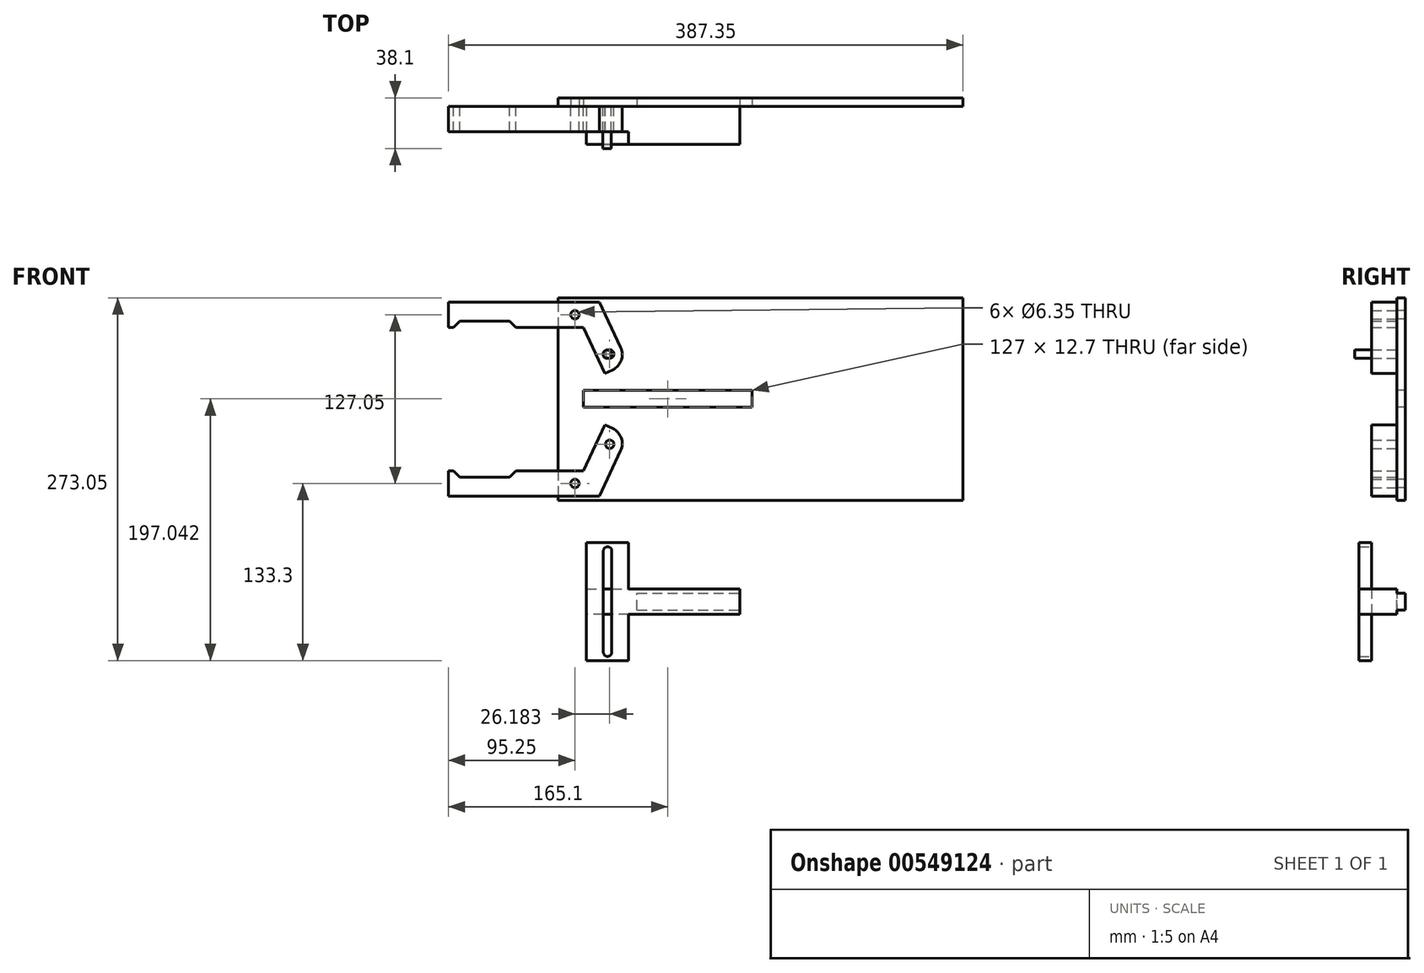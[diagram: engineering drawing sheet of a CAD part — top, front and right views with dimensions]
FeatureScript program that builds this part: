
annotation { "Feature Type Name" : "Feature", "Feature Type Description" : "" }
export const myFeature = defineFeature(function(context is Context, id is Id, definition is map)
    precondition{}
    {
        {
            var Q0;
            Q0=qCreatedBy(makeId("Front.planeOp"),FACE);
            var sketch = newSketch(context, id + "F0", { "sketchPlane" : qUnion([Q0])});
            skLineSegment(sketch, "E0.bottom", {"start": v(-95.25, 9.53) * mm, "end": v(18.49, 9.53) * mm});
            skLineSegment(sketch, "E0.top", {"start": v(-95.25, -9.52) * mm, "end": v(-91.44, -9.52) * mm});
            skLineSegment(sketch, "E0.left", {"start": v(-95.25, 9.53) * mm, "end": v(-95.25, -9.52) * mm});
            skLineSegment(sketch, "E1", {"start": v(6.35, -9.52) * mm, "end": v(22.5, -44.18) * mm});
            skLineSegment(sketch, "E2", {"start": v(22.5, -44.18) * mm, "end": v(39.77, -36.13) * mm});
            skLineSegment(sketch, "E3", {"start": v(18.49, 9.53) * mm, "end": v(39.77, -36.13) * mm});
            skCircle(sketch, "E4", {"center": v(0, 0) * mm, "radius": 3.18 * mm});
            skLineSegment(sketch, "E5", {"start": v(31.14, -40.15) * mm, "end": v(7.98, 9.53) * mm, "construction": true});
            skCircle(sketch, "E6", {"center": v(26.18, -29.52) * mm, "radius": 3.18 * mm});
            skLineSegment(sketch, "E7", {"start": v(-91.44, -9.53) * mm, "end": v(-86.6, -4.68) * mm});
            skLineSegment(sketch, "E8", {"start": v(-86.6, -4.68) * mm, "end": v(-49.3, -4.68) * mm});
            skLineSegment(sketch, "E9", {"start": v(-49.3, -4.68) * mm, "end": v(-44.45, -9.52) * mm});
            skLineSegment(sketch, "E10", {"start": v(-44.45, -9.52) * mm, "end": v(-44.45, -9.52) * mm});
            skLineSegment(sketch, "E11", {"start": v(-44.45, -9.52) * mm, "end": v(6.35, -9.52) * mm});
            skSolve(sketch);
        }
        {
            var Q0;
            Q0 = qSketchRegion(id + "F0", true);
            extrude(context, id + "F1", {"entities" : qUnion([Q0]), "depth" : 19.05 * mm, "offsetDistance" : 25.4 * mm});
        }
        {
            var Q0;
            Q0=qCreatedBy(makeId("Front.planeOp"),FACE);
            var sketch = newSketch(context, id + "F2", { "sketchPlane" : qUnion([Q0])});
            skLineSegment(sketch, "E12", {"start": v(0, 0) * mm, "end": v(0, -127) * mm, "construction": true});
            skLineSegment(sketch, "E13", {"start": v(0, -63.5) * mm, "end": v(127, -63.5) * mm, "construction": true});
            skSolve(sketch);
        }
        {
            var Q0;
            Q0=qCreatedBy(makeId("Top.planeOp"),FACE);
            cPlane(context, id + "F3", {"entities" : qUnion([Q0]), "cplaneType" : CPlaneType.OFFSET, "offset" : 63.5 * mm, "oppositeDirection" : true, "width" : 152.4 * mm, "height" : 152.4 * mm});
        }
        {
            var Q0;
            Q0=makeQuery(id+"F1.opExtrude","SWEPT_BODY",BODY,{"disambiguationData":[OSD([sQuery(id+"F0.wireOp",EDGE,"E0.bottom"),sQuery(id+"F0.wireOp",EDGE,"E0.top"),sQuery(id+"F0.wireOp",EDGE,"E0.left"),sQuery(id+"F0.wireOp",EDGE,"E1"),sQuery(id+"F0.wireOp",EDGE,"E2"),sQuery(id+"F0.wireOp",EDGE,"E3"),sQuery(id+"F0.wireOp",EDGE,"E4"),sQuery(id+"F0.wireOp",EDGE,"E6"),sQuery(id+"F0.wireOp",EDGE,"E7"),sQuery(id+"F0.wireOp",EDGE,"E8"),sQuery(id+"F0.wireOp",EDGE,"E9"),sQuery(id+"F0.wireOp",EDGE,"E11")])]});
            var Q1;
            Q1=qCreatedBy(id+"F3.planeOp",FACE);
            mirror(context, id + "F4", {"entities" : qUnion([Q0]), "mirrorPlane" : qUnion([Q1])});
        }
        {
            var Q0;
            Q0=qCreatedBy(makeId("Front.planeOp"),FACE);
            var sketch = newSketch(context, id + "F5", { "sketchPlane" : qUnion([Q0])});
            skLineSegment(sketch, "E14.bottom", {"start": v(-12.7, 12.7) * mm, "end": v(292.1, 12.7) * mm});
            skLineSegment(sketch, "E14.top", {"start": v(-12.7, -139.7) * mm, "end": v(292.1, -139.7) * mm});
            skLineSegment(sketch, "E14.left", {"start": v(-12.7, 12.7) * mm, "end": v(-12.7, -139.7) * mm});
            skLineSegment(sketch, "E14.right", {"start": v(292.1, 12.7) * mm, "end": v(292.1, -139.7) * mm});
            skLineSegment(sketch, "E15", {"start": v(-12.7, -63.5) * mm, "end": v(292.1, -63.5) * mm, "construction": true});
            skCircle(sketch, "E16", {"center": v(0, 0) * mm, "radius": 3.18 * mm});
            skCircle(sketch, "E17", {"center": v(0, -127.05) * mm, "radius": 3.18 * mm});
            skLineSegment(sketch, "E18.bottom", {"start": v(6.35, -56.96) * mm, "end": v(133.35, -56.96) * mm});
            skLineSegment(sketch, "E18.top", {"start": v(6.35, -69.66) * mm, "end": v(133.35, -69.66) * mm});
            skLineSegment(sketch, "E18.left", {"start": v(6.35, -56.96) * mm, "end": v(6.35, -69.66) * mm});
            skLineSegment(sketch, "E18.right", {"start": v(133.35, -56.96) * mm, "end": v(133.35, -69.66) * mm});
            skSolve(sketch);
        }
        {
            var Q0;
            Q0 = qSketchRegion(id + "F5", true);
            extrude(context, id + "F6", {"entities" : qUnion([Q0]), "oppositeDirection" : true, "depth" : 6.35 * mm, "offsetDistance" : 25.4 * mm});
        }
        {
            var Q0;
            Q0=makeQuery(id+"F6.opExtrude","CAP_FACE",FACE,{"disambiguationData":[OSD([sQuery(id+"F5.wireOp",EDGE,"E14.bottom"),sQuery(id+"F5.wireOp",EDGE,"E14.top"),sQuery(id+"F5.wireOp",EDGE,"E14.left"),sQuery(id+"F5.wireOp",EDGE,"E14.right"),sQuery(id+"F5.wireOp",EDGE,"E16"),sQuery(id+"F5.wireOp",EDGE,"E17")])],"isStart":true});
            cPlane(context, id + "F7", {"entities" : qUnion([Q0]), "cplaneType" : CPlaneType.OFFSET, "offset" : 19.05 * mm, "width" : 152.4 * mm, "height" : 152.4 * mm});
        }
        {
            var Q0;
            Q0=makeQuery(id+"F1.opExtrude","SWEPT_EDGE",EDGE,{"disambiguationData":[OSD([sQuery(id+"F0.wireOp",EDGE,"E2"),sQuery(id+"F0.wireOp",EDGE,"E3")])]});
            var Q1;
            Q1=makeQuery(id+"F4.opPattern","COPY",EDGE,{"derivedFrom":makeQuery(id+"F1.opExtrude","SWEPT_EDGE",EDGE,{"disambiguationData":[OSD([sQuery(id+"F0.wireOp",EDGE,"E2"),sQuery(id+"F0.wireOp",EDGE,"E3")])]}),"instanceName":"1"});
            fillet(context, id + "F8", {"entities" : qUnion([Q0, Q1]), "radius" : 12.7 * mm, "tangentPropagation" : true, "allowEdgeOverflow" : false});
        }
        {
            var Q0;
            Q0=makeQuery(id+"F6.opExtrude","CAP_FACE",FACE,{"disambiguationData":[OSD([sQuery(id+"F5.wireOp",EDGE,"E14.bottom"),sQuery(id+"F5.wireOp",EDGE,"E14.top"),sQuery(id+"F5.wireOp",EDGE,"E14.left"),sQuery(id+"F5.wireOp",EDGE,"E14.right"),sQuery(id+"F5.wireOp",EDGE,"E16"),sQuery(id+"F5.wireOp",EDGE,"E17"),sQuery(id+"F5.wireOp",EDGE,"E18.bottom"),sQuery(id+"F5.wireOp",EDGE,"E18.top"),sQuery(id+"F5.wireOp",EDGE,"E18.left"),sQuery(id+"F5.wireOp",EDGE,"E18.right")])],"isStart":true});
            var sketch = newSketch(context, id + "F9", { "sketchPlane" : qUnion([Q0])});
            skCircle(sketch, "E19", {"center": v(24.28, -29.72) * mm, "radius": 3.18 * mm});
            skSolve(sketch);
        }
        {
            var Q0;
            Q0 = qSketchRegion(id + "F9", true);
            extrude(context, id + "F10", {"entities" : qUnion([Q0]), "depth" : 31.75 * mm, "offsetDistance" : 25.4 * mm});
        }
        {
            var Q0;
            Q0=qCreatedBy(id+"F7.planeOp",FACE);
            var sketch = newSketch(context, id + "F11", { "sketchPlane" : qUnion([Q0])});
            skLineSegment(sketch, "E20.bottom", {"start": v(8.72, -171.45) * mm, "end": v(40.47, -171.45) * mm});
            skLineSegment(sketch, "E20.top", {"start": v(8.72, -260.35) * mm, "end": v(40.47, -260.35) * mm});
            skLineSegment(sketch, "E20.left", {"start": v(8.72, -171.45) * mm, "end": v(8.72, -260.35) * mm});
            skLineSegment(sketch, "E21", {"start": v(24.6, -171.45) * mm, "end": v(24.6, -260.35) * mm, "construction": true});
            skLineSegment(sketch, "E22", {"start": v(40.47, -53.98) * mm, "end": v(40.47, -53.98) * mm});
            skLineSegment(sketch, "E23", {"start": v(8.72, -215.9) * mm, "end": v(40.47, -215.9) * mm, "construction": true});
            skLineSegment(sketch, "E24", {"start": v(40.47, -171.45) * mm, "end": v(40.47, -206.38) * mm});
            skLineSegment(sketch, "E25", {"start": v(21.42, -215.9) * mm, "end": v(27.77, -215.9) * mm, "construction": true});
            skLineSegment(sketch, "E26", {"start": v(40.47, -171.45) * mm, "end": v(40.47, -171.45) * mm});
            skArc(sketch, "E27", {"start": v(27.77, -177.8) * mm, "mid": v(24.6, -174.62) * mm, "end": v(21.42, -177.8) * mm});
            skArc(sketch, "E28.MirrorC", {"start": v(27.77, -254) * mm, "mid": v(24.6, -257.18) * mm, "end": v(21.42, -254) * mm});
            skLineSegment(sketch, "E29", {"start": v(21.42, -177.8) * mm, "end": v(21.42, -177.8) * mm});
            skLineSegment(sketch, "E30", {"start": v(27.77, -177.8) * mm, "end": v(27.77, -177.8) * mm});
            skLineSegment(sketch, "E31", {"start": v(21.42, -254) * mm, "end": v(21.42, -254) * mm});
            skLineSegment(sketch, "E32", {"start": v(21.42, -177.8) * mm, "end": v(21.42, -254) * mm});
            skLineSegment(sketch, "E33", {"start": v(27.77, -177.8) * mm, "end": v(27.77, -254) * mm});
            skLineSegment(sketch, "E34", {"start": v(40.47, -206.38) * mm, "end": v(124.06, -206.38) * mm});
            skLineSegment(sketch, "E35.MirrorCS", {"start": v(40.47, -225.43) * mm, "end": v(124.06, -225.43) * mm});
            skLineSegment(sketch, "E36", {"start": v(124.06, -206.38) * mm, "end": v(124.06, -225.43) * mm});
            skLineSegment(sketch, "E37.trimOffspring", {"start": v(40.47, -225.43) * mm, "end": v(40.47, -260.35) * mm});
            skLineSegment(sketch, "E38", {"start": v(40.47, -225.43) * mm, "end": v(8.72, -225.43) * mm});
            skLineSegment(sketch, "E39", {"start": v(40.47, -206.38) * mm, "end": v(8.72, -206.38) * mm});
            skLineSegment(sketch, "E40", {"start": v(8.72, -212.72) * mm, "end": v(124.06, -212.72) * mm});
            skLineSegment(sketch, "E41.MirrorCS", {"start": v(8.72, -219.08) * mm, "end": v(124.06, -219.08) * mm});
            skSolve(sketch);
        }
        {
            var Q0;
            {var subQ6=sQuery(id+"F11.wireOp",EDGE,"E20.top");Q0=makeQuery(id+"F11.imprint","IMPRINT",FACE,{"disambiguationData":[TD([[makeQuery(id+"F11.imprint","IMPRINT",EDGE,{"derivedFrom":subQ6}),1.0]])]});}
            var Q1;
            {var subQ6=sQuery(id+"F11.wireOp",EDGE,"E20.bottom");Q1=makeQuery(id+"F11.imprint","IMPRINT",FACE,{"disambiguationData":[TD([[makeQuery(id+"F11.imprint","IMPRINT",EDGE,{"derivedFrom":subQ6}),-1.0]])]});}
            var Q2;
            {var subQ1=sQuery(id+"F11.wireOp",EDGE,"E34");Q2=makeQuery(id+"F11.imprint","IMPRINT",FACE,{"disambiguationData":[TD([[makeQuery(id+"F11.imprint","IMPRINT",EDGE,{"derivedFrom":subQ1}),-1.0]])]});}
            var Q3;
            {var subQ0=sQuery(id+"F11.wireOp",EDGE,"E39");var subQ1=sQuery(id+"F11.wireOp",EDGE,"E20.left");var subQ2=makeQuery(id+"F11.imprint","INTERSECT",VERTEX,{"derivedFrom":[subQ1,subQ0]});Q3=makeQuery(id+"F11.imprint","IMPRINT",FACE,{"disambiguationData":[TD([[makeQuery(id+"F11.imprint","IMPRINT",EDGE,{"disambiguationData":[TD([[subQ2,-1.0]])],"derivedFrom":subQ1}),1.0]])]});}
            var Q4;
            {var subQ0=sQuery(id+"F11.wireOp",EDGE,"E38");var subQ1=sQuery(id+"F11.wireOp",EDGE,"E20.left");var subQ2=makeQuery(id+"F11.imprint","INTERSECT",VERTEX,{"derivedFrom":[subQ1,subQ0]});Q4=makeQuery(id+"F11.imprint","IMPRINT",FACE,{"disambiguationData":[TD([[makeQuery(id+"F11.imprint","IMPRINT",EDGE,{"disambiguationData":[TD([[subQ2,1.0]])],"derivedFrom":subQ1}),1.0]])]});}
            var Q5;
            {var subQ1=sQuery(id+"F11.wireOp",EDGE,"E35.MirrorCS");Q5=makeQuery(id+"F11.imprint","IMPRINT",FACE,{"disambiguationData":[TD([[makeQuery(id+"F11.imprint","IMPRINT",EDGE,{"derivedFrom":subQ1}),1.0]])]});}
            var Q6;
            {var subQ0=sQuery(id+"F11.wireOp",EDGE,"E40");var subQ1=sQuery(id+"F11.wireOp",EDGE,"E33");var subQ2=makeQuery(id+"F11.imprint","INTERSECT",VERTEX,{"derivedFrom":[subQ1,subQ0]});Q6=makeQuery(id+"F11.imprint","IMPRINT",FACE,{"disambiguationData":[TD([[makeQuery(id+"F11.imprint","IMPRINT",EDGE,{"disambiguationData":[TD([[subQ2,-1.0]])],"derivedFrom":subQ1}),1.0]])]});}
            var Q7;
            {var subQ0=sQuery(id+"F11.wireOp",EDGE,"E40");var subQ1=sQuery(id+"F11.wireOp",EDGE,"E20.left");var subQ2=makeQuery(id+"F11.imprint","INTERSECT",VERTEX,{"derivedFrom":[subQ1,subQ0]});Q7=makeQuery(id+"F11.imprint","IMPRINT",FACE,{"disambiguationData":[TD([[makeQuery(id+"F11.imprint","IMPRINT",EDGE,{"disambiguationData":[TD([[subQ2,-1.0]])],"derivedFrom":subQ1}),1.0]])]});}
            extrude(context, id + "F12", {"entities" : qUnion([Q0, Q1, Q2, Q3, Q4, Q5, Q6, Q7]), "depth" : 9.52 * mm, "offsetDistance" : 25.4 * mm});
        }
        {
            var Q0;
            {var subQ1=sQuery(id+"F11.wireOp",EDGE,"E35.MirrorCS");Q0=makeQuery(id+"F11.imprint","IMPRINT",FACE,{"disambiguationData":[TD([[makeQuery(id+"F11.imprint","IMPRINT",EDGE,{"derivedFrom":subQ1}),1.0]])]});}
            var Q1;
            {var subQ0=sQuery(id+"F11.wireOp",EDGE,"E40");var subQ1=sQuery(id+"F11.wireOp",EDGE,"E33");var subQ2=makeQuery(id+"F11.imprint","INTERSECT",VERTEX,{"derivedFrom":[subQ1,subQ0]});Q1=makeQuery(id+"F11.imprint","IMPRINT",FACE,{"disambiguationData":[TD([[makeQuery(id+"F11.imprint","IMPRINT",EDGE,{"disambiguationData":[TD([[subQ2,-1.0]])],"derivedFrom":subQ1}),1.0]])]});}
            var Q2;
            {var subQ1=sQuery(id+"F11.wireOp",EDGE,"E34");Q2=makeQuery(id+"F11.imprint","IMPRINT",FACE,{"disambiguationData":[TD([[makeQuery(id+"F11.imprint","IMPRINT",EDGE,{"derivedFrom":subQ1}),-1.0]])]});}
            var Q3;
            {var subQ0=sQuery(id+"F11.wireOp",EDGE,"E39");var subQ1=sQuery(id+"F11.wireOp",EDGE,"E20.left");var subQ2=makeQuery(id+"F11.imprint","INTERSECT",VERTEX,{"derivedFrom":[subQ1,subQ0]});Q3=makeQuery(id+"F11.imprint","IMPRINT",FACE,{"disambiguationData":[TD([[makeQuery(id+"F11.imprint","IMPRINT",EDGE,{"disambiguationData":[TD([[subQ2,-1.0]])],"derivedFrom":subQ1}),1.0]])]});}
            var Q4;
            {var subQ0=sQuery(id+"F11.wireOp",EDGE,"E38");var subQ1=sQuery(id+"F11.wireOp",EDGE,"E20.left");var subQ2=makeQuery(id+"F11.imprint","INTERSECT",VERTEX,{"derivedFrom":[subQ1,subQ0]});Q4=makeQuery(id+"F11.imprint","IMPRINT",FACE,{"disambiguationData":[TD([[makeQuery(id+"F11.imprint","IMPRINT",EDGE,{"disambiguationData":[TD([[subQ2,1.0]])],"derivedFrom":subQ1}),1.0]])]});}
            var Q5;
            {var subQ0=sQuery(id+"F11.wireOp",EDGE,"E40");var subQ1=sQuery(id+"F11.wireOp",EDGE,"E20.left");var subQ2=makeQuery(id+"F11.imprint","INTERSECT",VERTEX,{"derivedFrom":[subQ1,subQ0]});Q5=makeQuery(id+"F11.imprint","IMPRINT",FACE,{"disambiguationData":[TD([[makeQuery(id+"F11.imprint","IMPRINT",EDGE,{"disambiguationData":[TD([[subQ2,-1.0]])],"derivedFrom":subQ1}),1.0]])]});}
            var Q6;
            {var subQ0=sQuery(id+"F11.wireOp",EDGE,"E40");var subQ1=sQuery(id+"F11.wireOp",EDGE,"E32");var subQ2=makeQuery(id+"F11.imprint","INTERSECT",VERTEX,{"derivedFrom":[subQ1,subQ0]});Q6=makeQuery(id+"F11.imprint","IMPRINT",FACE,{"disambiguationData":[TD([[makeQuery(id+"F11.imprint","IMPRINT",EDGE,{"disambiguationData":[TD([[subQ2,-1.0]])],"derivedFrom":subQ1}),1.0]])]});}
            var Q7;
            {var subQ0=sQuery(id+"F11.wireOp",EDGE,"E39");var subQ1=sQuery(id+"F11.wireOp",EDGE,"E32");var subQ2=makeQuery(id+"F11.imprint","INTERSECT",VERTEX,{"derivedFrom":[subQ1,subQ0]});Q7=makeQuery(id+"F11.imprint","IMPRINT",FACE,{"disambiguationData":[TD([[makeQuery(id+"F11.imprint","IMPRINT",EDGE,{"disambiguationData":[TD([[subQ2,-1.0]])],"derivedFrom":subQ1}),1.0]])]});}
            var Q8;
            {var subQ0=sQuery(id+"F11.wireOp",EDGE,"E41.MirrorCS");var subQ1=sQuery(id+"F11.wireOp",EDGE,"E32");var subQ2=makeQuery(id+"F11.imprint","INTERSECT",VERTEX,{"derivedFrom":[subQ1,subQ0]});Q8=makeQuery(id+"F11.imprint","IMPRINT",FACE,{"disambiguationData":[TD([[makeQuery(id+"F11.imprint","IMPRINT",EDGE,{"disambiguationData":[TD([[subQ2,-1.0]])],"derivedFrom":subQ1}),1.0]])]});}
            extrude(context, id + "F13", {"entities" : qUnion([Q0, Q1, Q2, Q3, Q4, Q5, Q6, Q7, Q8]), "operationType" : NewBodyOperationType.ADD, "oppositeDirection" : true, "depth" : 19.05 * mm, "offsetDistance" : 25.4 * mm});
        }
        {
            var Q0;
            Q0=makeQuery(id+"F13.opExtrude","CAP_FACE",FACE,{"disambiguationData":[OSD([sQuery(id+"F11.wireOp",EDGE,"E20.left"),sQuery(id+"F11.wireOp",EDGE,"E34"),sQuery(id+"F11.wireOp",EDGE,"E35.MirrorCS"),sQuery(id+"F11.wireOp",EDGE,"E36"),sQuery(id+"F11.wireOp",EDGE,"E38"),sQuery(id+"F11.wireOp",EDGE,"E39")])],"isStart":false});
            var sketch = newSketch(context, id + "F14", { "sketchPlane" : qUnion([Q0])});
            skLineSegment(sketch, "E42", {"start": v(-124.06, -215.9) * mm, "end": v(-8.72, -215.9) * mm, "construction": true});
            skLineSegment(sketch, "E43.bottom", {"start": v(-46.82, -222.25) * mm, "end": v(-124.06, -222.25) * mm});
            skLineSegment(sketch, "E43.top", {"start": v(-46.82, -209.55) * mm, "end": v(-124.06, -209.55) * mm});
            skLineSegment(sketch, "E43.right", {"start": v(-124.06, -222.25) * mm, "end": v(-124.06, -209.55) * mm});
            skLineSegment(sketch, "E44", {"start": v(-46.82, -222.25) * mm, "end": v(-46.82, -209.55) * mm});
            skSolve(sketch);
        }
        {
            var Q0;
            Q0 = qSketchRegion(id + "F14", true);
            extrude(context, id + "F15", {"entities" : qUnion([Q0]), "operationType" : NewBodyOperationType.ADD, "depth" : 6.35 * mm, "offsetDistance" : 25.4 * mm});
        }
    });
